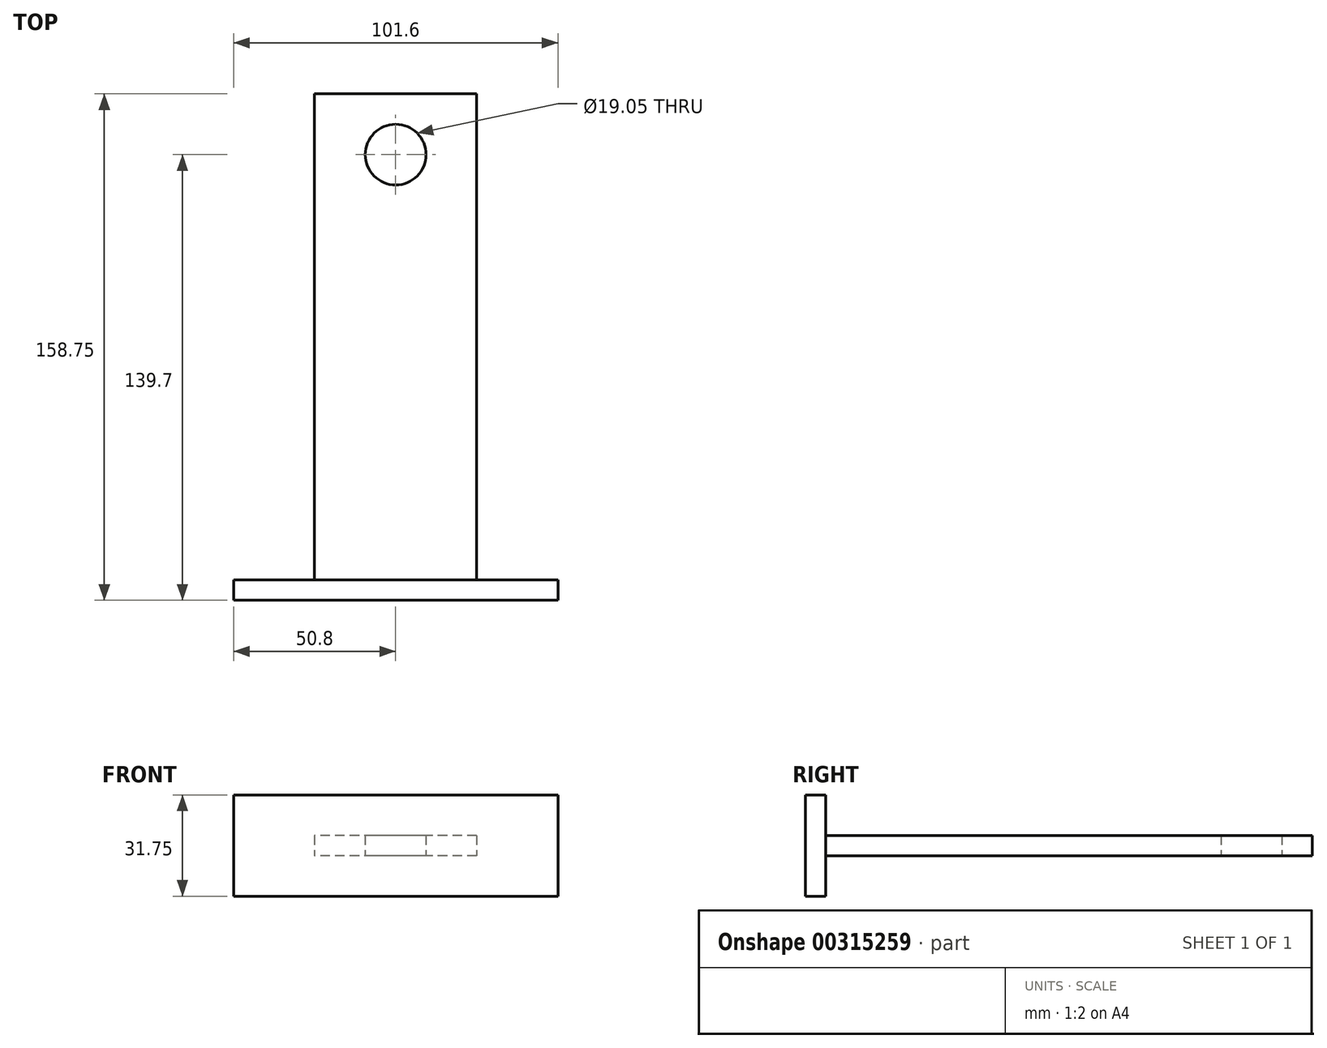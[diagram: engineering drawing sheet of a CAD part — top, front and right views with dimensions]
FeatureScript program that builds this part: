
annotation { "Feature Type Name" : "Feature", "Feature Type Description" : "" }
export const myFeature = defineFeature(function(context is Context, id is Id, definition is map)
    precondition{}
    {
        {
            var Q0;
            Q0=qCreatedBy(makeId("Right.planeOp"),FACE);
            var sketch = newSketch(context, id + "F0", { "sketchPlane" : qUnion([Q0])});
            skLineSegment(sketch, "E0.bottom", {"start": v(-63.22, 12.45) * mm, "end": v(89.18, 12.45) * mm});
            skLineSegment(sketch, "E0.top", {"start": v(-63.22, 6.1) * mm, "end": v(89.18, 6.1) * mm});
            skLineSegment(sketch, "E0.left", {"start": v(-63.22, 12.45) * mm, "end": v(-63.22, 6.1) * mm});
            skLineSegment(sketch, "E0.right", {"start": v(89.18, 12.45) * mm, "end": v(89.18, 6.1) * mm});
            skSolve(sketch);
        }
        {
            var Q0;
            Q0=makeQuery(id+"F0.imprint","IMPRINT",FACE,{"disambiguationData":[TD([[makeQuery(id+"F0.imprint","IMPRINT",EDGE,{"derivedFrom":sQuery(id+"F0.wireOp",EDGE,"E0.bottom")}),-1.0]])]});
            extrude(context, id + "F1", {"entities" : qUnion([Q0]), "depth" : 50.8 * mm});
        }
        {
            var Q0;
            Q0=qCreatedBy(makeId("Right.planeOp"),FACE);
            var sketch = newSketch(context, id + "F2", { "sketchPlane" : qUnion([Q0])});
            skLineSegment(sketch, "E1", {"start": v(-63.22, 12.45) * mm, "end": v(-63.22, 25.15) * mm});
            skLineSegment(sketch, "E2", {"start": v(-63.22, 25.15) * mm, "end": v(-69.57, 25.15) * mm});
            skLineSegment(sketch, "E3", {"start": v(-69.57, 25.15) * mm, "end": v(-69.57, -6.6) * mm});
            skLineSegment(sketch, "E4", {"start": v(-69.57, -6.6) * mm, "end": v(-63.22, -6.6) * mm});
            skLineSegment(sketch, "E5", {"start": v(-63.22, -6.6) * mm, "end": v(-63.22, 12.45) * mm});
            skSolve(sketch);
        }
        {
            var Q0;
            Q0 = qSketchRegion(id + "F2", true);
            extrude(context, id + "F3", {"entities" : qUnion([Q0]), "operationType" : NewBodyOperationType.ADD, "depth" : 76.2 * mm, "hasSecondDirection" : true, "secondDirectionOppositeDirection" : true, "secondDirectionDepth" : 25.4 * mm});
        }
        {
            var Q0;
            Q0=qCreatedBy(makeId("Top.planeOp"),FACE);
            var sketch = newSketch(context, id + "F4", { "sketchPlane" : qUnion([Q0])});
            skLineSegment(sketch, "E6", {"start": v(25.4, 95.76) * mm, "end": v(25.4, -81.46) * mm, "construction": true});
            skCircle(sketch, "E7", {"center": v(25.4, 70.13) * mm, "radius": 9.53 * mm});
            skSolve(sketch);
        }
        {
            var Q0;
            Q0 = qSketchRegion(id + "F4", true);
            extrude(context, id + "F5", {"entities" : qUnion([Q0]), "operationType" : NewBodyOperationType.REMOVE, "endBound" : BoundingType.THROUGH_ALL, "depth" : 25.4 * mm});
        }
    });
